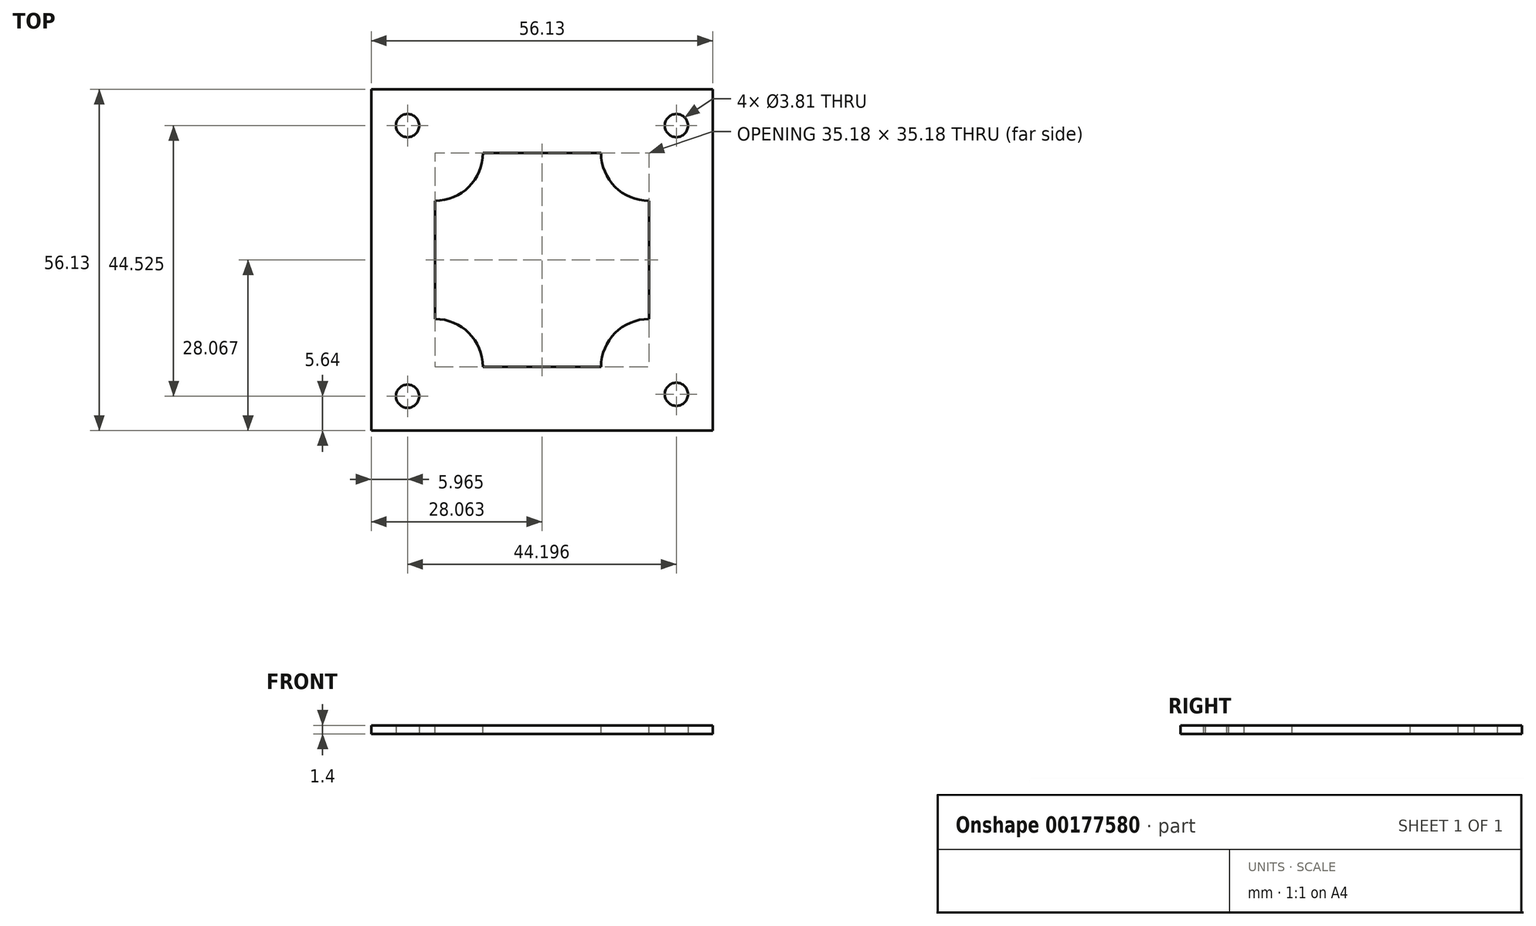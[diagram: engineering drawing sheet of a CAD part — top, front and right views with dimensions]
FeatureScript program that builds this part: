
annotation { "Feature Type Name" : "Feature", "Feature Type Description" : "" }
export const myFeature = defineFeature(function(context is Context, id is Id, definition is map)
    precondition{}
    {
        {
            var Q0;
            Q0=qCreatedBy(makeId("Top.planeOp"),FACE);
            var sketch = newSketch(context, id + "F0", { "sketchPlane" : qUnion([Q0])});
            skLineSegment(sketch, "E0.bottom", {"start": v(0, 0) * mm, "end": v(-56.13, 0) * mm});
            skLineSegment(sketch, "E0.top", {"start": v(0, 56.13) * mm, "end": v(-56.13, 56.13) * mm});
            skLineSegment(sketch, "E0.left", {"start": v(0, 0) * mm, "end": v(0, 56.13) * mm});
            skLineSegment(sketch, "E0.right", {"start": v(-56.13, 0) * mm, "end": v(-56.13, 56.13) * mm});
            skCircle(sketch, "E1", {"center": v(-50.17, 50.16) * mm, "radius": 1.9 * mm});
            skCircle(sketch, "E2", {"center": v(-5.97, 50.16) * mm, "radius": 1.9 * mm});
            skCircle(sketch, "E3", {"center": v(-50.17, 5.64) * mm, "radius": 1.9 * mm});
            skCircle(sketch, "E4", {"center": v(-5.97, 5.97) * mm, "radius": 1.9 * mm});
            skSolve(sketch);
        }
        {
            var Q0;
            Q0=makeQuery(id+"F0.imprint","IMPRINT",FACE,{"disambiguationData":[TD([[makeQuery(id+"F0.imprint","IMPRINT",EDGE,{"derivedFrom":sQuery(id+"F0.wireOp",EDGE,"E0.bottom")}),-1.0]])]});
            extrude(context, id + "F1", {"entities" : qUnion([Q0]), "depth" : 1.4 * mm});
        }
        {
            var Q0;
            Q0=makeQuery(id+"F1.opExtrude","CAP_FACE",FACE,{"disambiguationData":[OSD([sQuery(id+"F0.wireOp",EDGE,"E0.bottom"),sQuery(id+"F0.wireOp",EDGE,"E0.top"),sQuery(id+"F0.wireOp",EDGE,"E0.left"),sQuery(id+"F0.wireOp",EDGE,"E0.right"),sQuery(id+"F0.wireOp",EDGE,"E1"),sQuery(id+"F0.wireOp",EDGE,"E2"),sQuery(id+"F0.wireOp",EDGE,"E3"),sQuery(id+"F0.wireOp",EDGE,"E4")])],"isStart":false});
            var sketch = newSketch(context, id + "F2", { "sketchPlane" : qUnion([Q0])});
            skLineSegment(sketch, "E5.bottom", {"start": v(-45.66, 45.66) * mm, "end": v(-10.48, 45.66) * mm});
            skLineSegment(sketch, "E5.top", {"start": v(-45.66, 10.48) * mm, "end": v(-10.48, 10.48) * mm});
            skLineSegment(sketch, "E5.left", {"start": v(-45.66, 45.66) * mm, "end": v(-45.66, 10.48) * mm});
            skLineSegment(sketch, "E5.right", {"start": v(-10.48, 45.66) * mm, "end": v(-10.48, 10.48) * mm});
            skArc(sketch, "E6", {"start": v(-18.35, 45.66) * mm, "mid": v(-16.05, 40.09) * mm, "end": v(-10.48, 37.78) * mm});
            skArc(sketch, "E7", {"start": v(-37.78, 45.66) * mm, "mid": v(-40.09, 40.09) * mm, "end": v(-45.66, 37.78) * mm});
            skArc(sketch, "E8", {"start": v(-45.66, 18.35) * mm, "mid": v(-40.09, 16.05) * mm, "end": v(-37.78, 10.48) * mm});
            skArc(sketch, "E9", {"start": v(-18.35, 10.48) * mm, "mid": v(-16.05, 16.05) * mm, "end": v(-10.48, 18.35) * mm});
            skSolve(sketch);
        }
        {
            var Q0;
            {var subQ5=sQuery(id+"F2.wireOp",EDGE,"E6");Q0=makeQuery(id+"F2.imprint","IMPRINT",FACE,{"disambiguationData":[TD([[makeQuery(id+"F2.imprint","IMPRINT",EDGE,{"derivedFrom":subQ5}),-1.0]])]});}
            extrude(context, id + "F3", {"entities" : qUnion([Q0]), "operationType" : NewBodyOperationType.REMOVE, "oppositeDirection" : true, "depth" : 25.4 * mm});
        }
    });
